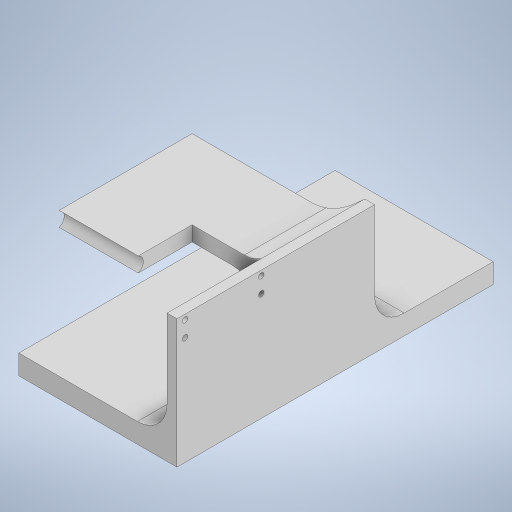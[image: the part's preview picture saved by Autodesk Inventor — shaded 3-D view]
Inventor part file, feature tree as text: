
AUTODESK INVENTOR PART (.ipt)
format: ipt  version: 2024.2 (Build 282272000, 272)  size: 296,448 bytes
history: native  units: in
note: dims shown in document units (in); Inventor stores cm internally (conversion verified against a paired STEP export)
features: extrude x7, sketch x7, fillet x3
ambient origin geometry x8: Origin, YZ Plane, XZ Plane, XY Plane, X Axis, Y Axis, Z Axis, Center Point
bodies: Solid1 (feature_tree)
feature tree (17):
  extrude  "Extrusion1"  Depth=0.75in
  extrude  "Extrusion2"  Depth=0.138in
  extrude  "Extrusion3"  Depth=0.3937in
  extrude  "Extrusion4"  Depth=1.0in TaperAngle=0.0deg
  fillet  "Fillet1"  Radius=0.138in
  fillet  "Fillet2"  Radius=1.929in
  extrude  "Extrusion5"  Depth=2.0in TaperAngle=0.0deg
  extrude  "Extrusion6"  Depth=4.0in
  extrude  "Extrusion7"  Depth=0.75in
  fillet  "Fillet3"  Radius=0.75in
  sketch  "Sketch1"  dims[d0=0.75in d1=5.0in]
  sketch  "Sketch2"  dims[d2=0.25in d3=0.0in d4=0.138in]
  sketch  "Sketch3"  dims[d5=0.138in d6=0.3937in]
  sketch  "Sketch4"  dims[d7=0.125in d8=1.0in d9=0.0in d11=0.138in d12=1.929in]
  sketch  "Sketch5"  dims[d13=0.138in d14=2.0in d15=0.0in]
  sketch  "Sketch6"  dims[d16=8.0in d17=4.0in]
  sketch  "Sketch7"  dims[d18=0.5in d19=0.0in d20=0.75in d21=0.75in d22=0.375in d23=2.0in d26=0.197in d27=0.25in d28=3.75in d29=0.0in d30=2.0in d31=1.5in d32=0.0in d33=0.2in d34=1.5in d35=0.0in d36=0.75in]
